# Revit family: Faucet-Spray_Kit-KOHLER-Elate-K-97258IN_1
name_source: partatom
category: Plumbing Fixtures
units: mm (PartAtom-declared; Revit-internal decimal feet)

## family parameters
Cut with Voids When Loaded = No
Host = Face
Maintain Annotation Orientation = No
OmniClass Number = 23.31.11.00
OmniClass Title = Faucets
Part Type = Normal
Room Calculation Point = No
Round Connector Dimension = Use Diameter
Shared = No

## types (5) — shared parameters
ADA Compliant = No
Assembly Code = D2010
CW Connection = No
Cold Water Inlet = Cold Water Inlet
Date Modified = 02/17/2022
Default Elevation = 36"
Description = Health Faucet With Hose & Bracket
Drain Included = No
Flow Rate = 0 GPM
HW Connection = Yes
Height = 6 3/4"
Hot Water Inlet = Hot Water Inlet
Length = 2 5/8"
Manufacturer = KOHLER Co.
Master Format 2014 = 22 41 39
Master Format 2014 Name = Residential Faucets, Supplies, and Trim
Material = Premium Metal Construction
Pressure = 0.00 psi
Product Name = Elate
Product Page URL = https://www.kohler.co.in
Tempered Water Inlet = Tempered Water Inlet
URL = https://www.kohler.co.in
Vent Connection = No
Waste Connection = No
Waste Water Outlet = Waste Water Outlet
WaterSense Certified = No
Width = 1 7/8"

## per-type parameters (varying)
| type | Finish | Model | Type |
| CP-Polished Chrome | Kohler-Metal-CP-Polished_Chrome | K-97258IN-CP | 5 |
| AF-French Gold | Kohler-Metal-AF-Vibrant_French_Gold | K-97258IN-AF | 1 |
| BL-Matte Black | Kohler-Metal-BL-Matte_Black | K-97258IN-BL | 2 |
| BN-Brushed Nickel | Kohler-Metal-BN-Vibrant_Brushed_Nickel | K-97258IN-BN | 3 |
| BV-Brushed Bronze | Kohler-Metal-BV-Brushed_Bronze | K-97258IN-BV | 4 |

## geometry (parser evidence)
native form markers: Sweep x5
no freeform markers — native parametric forms only
